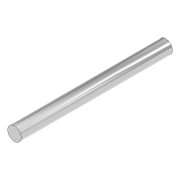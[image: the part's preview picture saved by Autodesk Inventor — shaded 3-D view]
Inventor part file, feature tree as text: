
AUTODESK INVENTOR PART (.ipt)
format: ipt  version: 2020 (Build 240168000, 168)  size: 76,800 bytes
history: native  units: in
note: dims shown in document units (in); Inventor stores cm internally (conversion verified against a paired STEP export)
features: extrude x1, sketch x1
ambient origin geometry x8: Origin, YZ Plane, XZ Plane, XY Plane, X Axis, Y Axis, Z Axis, Center Point
bodies: Solid1 (feature_tree)
feature tree (2):
  extrude  "Extrusion1"  Depth=2.185in TaperAngle=0.0deg
  sketch  "Sketch1"  dims[d0=0.1969in d1=2.185in d2=0.0in]
